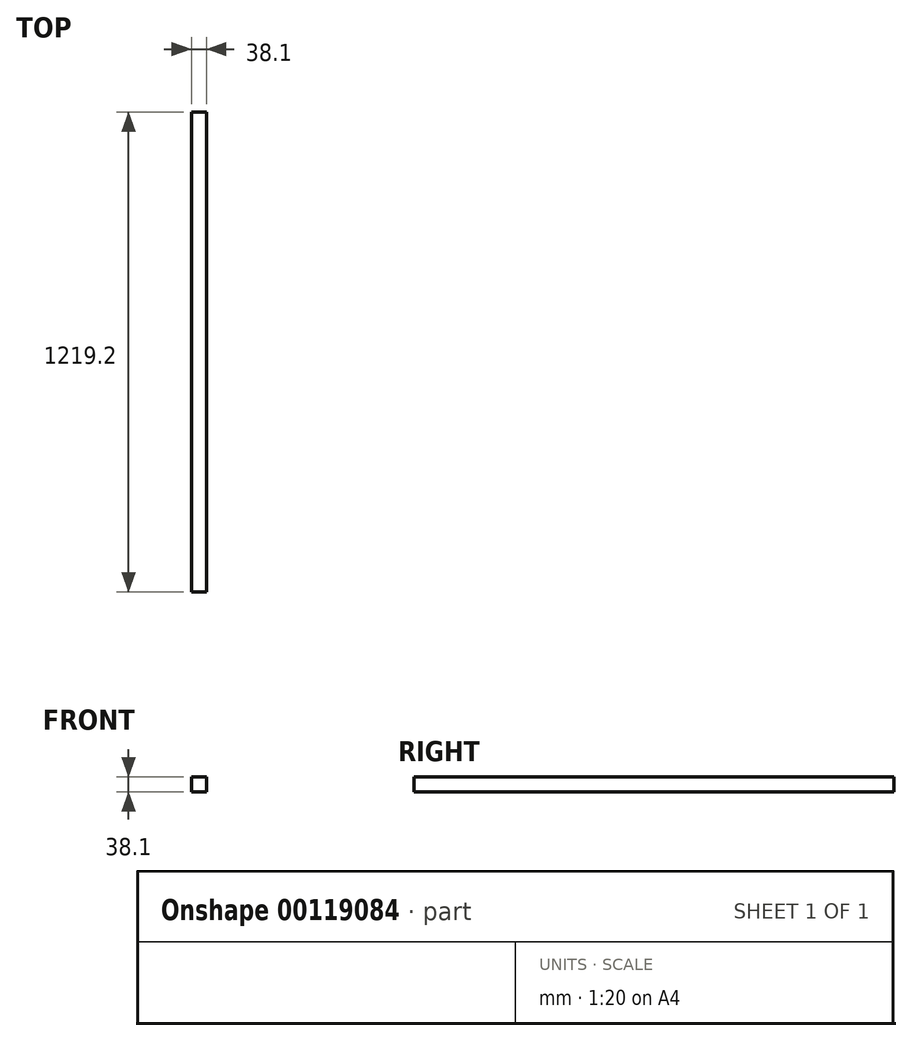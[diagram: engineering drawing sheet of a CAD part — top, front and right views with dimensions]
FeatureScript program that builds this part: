
annotation { "Feature Type Name" : "Feature", "Feature Type Description" : "" }
export const myFeature = defineFeature(function(context is Context, id is Id, definition is map)
    precondition{}
    {
        {
            var Q0;
            Q0=qCreatedBy(makeId("Front.planeOp"),FACE);
            var sketch = newSketch(context, id + "F0", { "sketchPlane" : qUnion([Q0])});
            skLineSegment(sketch, "E0.bottom", {"start": v(0, 0) * mm, "end": v(38.1, 0) * mm});
            skLineSegment(sketch, "E0.top", {"start": v(0, 38.1) * mm, "end": v(38.1, 38.1) * mm});
            skLineSegment(sketch, "E0.left", {"start": v(0, 0) * mm, "end": v(0, 38.1) * mm});
            skLineSegment(sketch, "E0.right", {"start": v(38.1, 0) * mm, "end": v(38.1, 38.1) * mm});
            skSolve(sketch);
        }
        {
            var Q0;
            Q0=makeQuery(id+"F0.imprint","IMPRINT",FACE,{"disambiguationData":[TD([[makeQuery(id+"F0.imprint","IMPRINT",EDGE,{"derivedFrom":sQuery(id+"F0.wireOp",EDGE,"E0.bottom")}),1.0]])]});
            extrude(context, id + "F1", {"entities" : qUnion([Q0]), "oppositeDirection" : true, "depth" : 1219.2 * mm});
        }
    });
